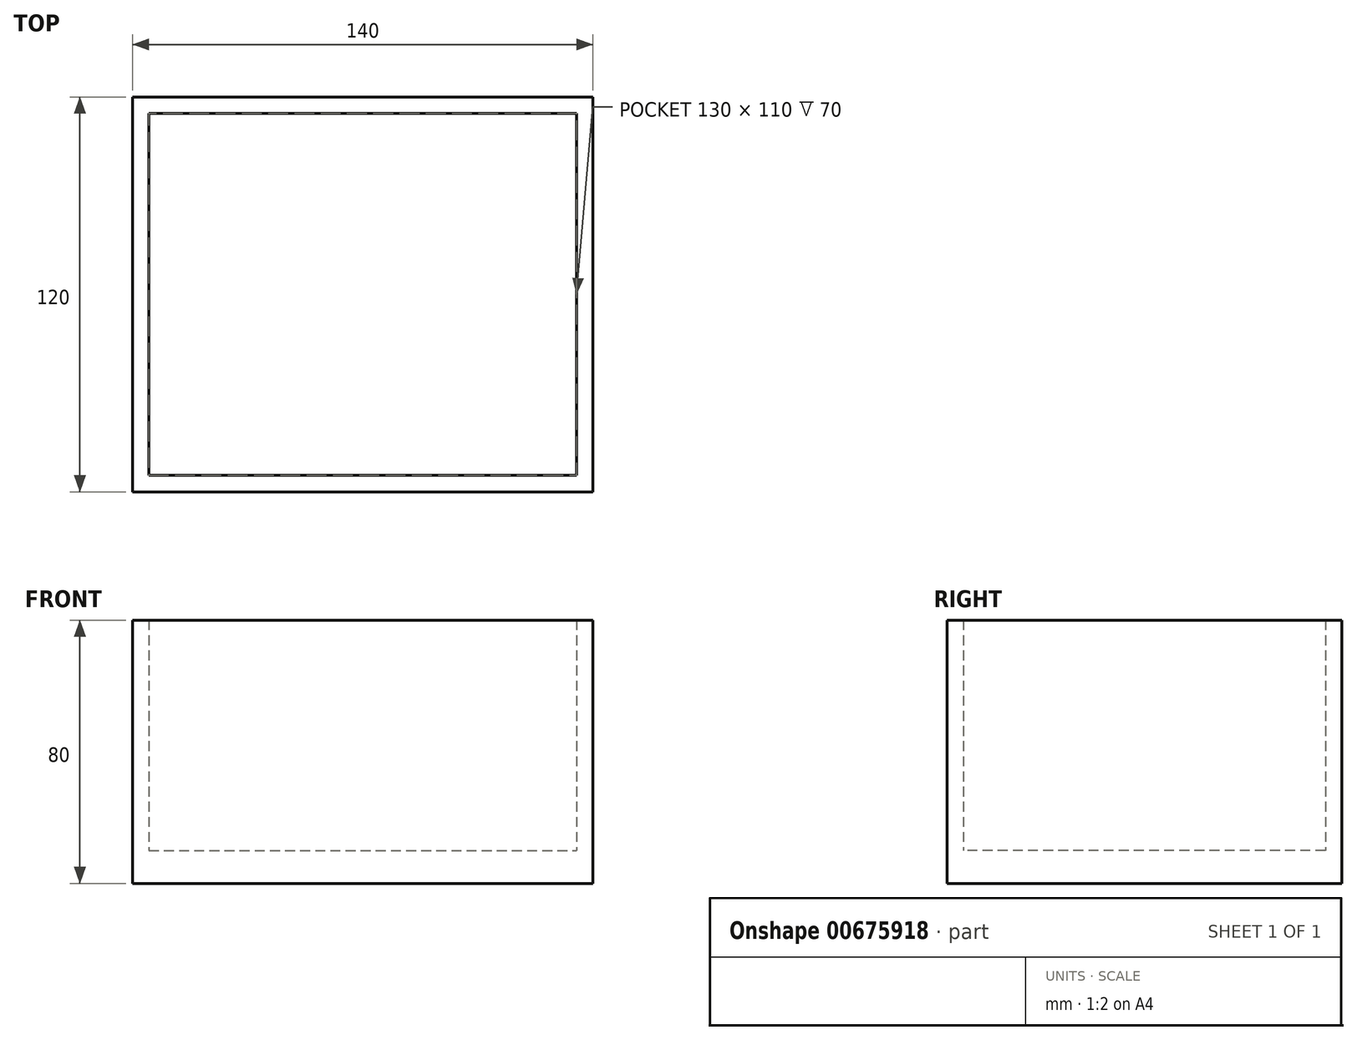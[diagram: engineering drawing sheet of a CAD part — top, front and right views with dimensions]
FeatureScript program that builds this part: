
annotation { "Feature Type Name" : "Feature", "Feature Type Description" : "" }
export const myFeature = defineFeature(function(context is Context, id is Id, definition is map)
    precondition{}
    {
        {
            var Q0;
            Q0=qCreatedBy(makeId("Top.planeOp"),FACE);
            var sketch = newSketch(context, id + "F0", { "sketchPlane" : qUnion([Q0])});
            skLineSegment(sketch, "E0.bottom", {"start": v(0, 0) * mm, "end": v(-140, 0) * mm});
            skLineSegment(sketch, "E0.top", {"start": v(0, 120) * mm, "end": v(-140, 120) * mm});
            skLineSegment(sketch, "E0.left", {"start": v(0, 0) * mm, "end": v(0, 120) * mm});
            skLineSegment(sketch, "E0.right", {"start": v(-140, 0) * mm, "end": v(-140, 120) * mm});
            skSolve(sketch);
        }
        {
            var Q0;
            Q0 = qSketchRegion(id + "F0", true);
            extrude(context, id + "F1", {"entities" : qUnion([Q0]), "depth" : 10 * mm, "offsetDistance" : 25 * mm});
        }
        {
            var Q0;
            Q0=makeQuery(id+"F1.opExtrude","CAP_FACE",FACE,{"disambiguationData":[OSD([sQuery(id+"F0.wireOp",EDGE,"E0.bottom"),sQuery(id+"F0.wireOp",EDGE,"E0.top"),sQuery(id+"F0.wireOp",EDGE,"E0.left"),sQuery(id+"F0.wireOp",EDGE,"E0.right")])],"isStart":false});
            var sketch = newSketch(context, id + "F2", { "sketchPlane" : qUnion([Q0])});
            skLineSegment(sketch, "E1.bottom", {"start": v(-140, 120) * mm, "end": v(0, 120) * mm});
            skLineSegment(sketch, "E1.top", {"start": v(-140, 0) * mm, "end": v(0, 0) * mm});
            skLineSegment(sketch, "E1.left", {"start": v(-140, 120) * mm, "end": v(-140, 0) * mm});
            skLineSegment(sketch, "E1.right", {"start": v(0, 120) * mm, "end": v(0, 0) * mm});
            skLineSegment(sketch, "E2.0", {"start": v(-135, 115) * mm, "end": v(-5, 115) * mm});
            skLineSegment(sketch, "E2.1", {"start": v(-135, 115) * mm, "end": v(-135, 5) * mm});
            skLineSegment(sketch, "E2.2", {"start": v(-135, 5) * mm, "end": v(-5, 5) * mm});
            skLineSegment(sketch, "E2.3", {"start": v(-5, 115) * mm, "end": v(-5, 5) * mm});
            skSolve(sketch);
        }
        {
            var Q0;
            Q0 = qSketchRegion(id + "F2", true);
            extrude(context, id + "F3", {"entities" : qUnion([Q0]), "operationType" : NewBodyOperationType.ADD, "depth" : 70 * mm, "offsetDistance" : 25 * mm});
        }
    });
